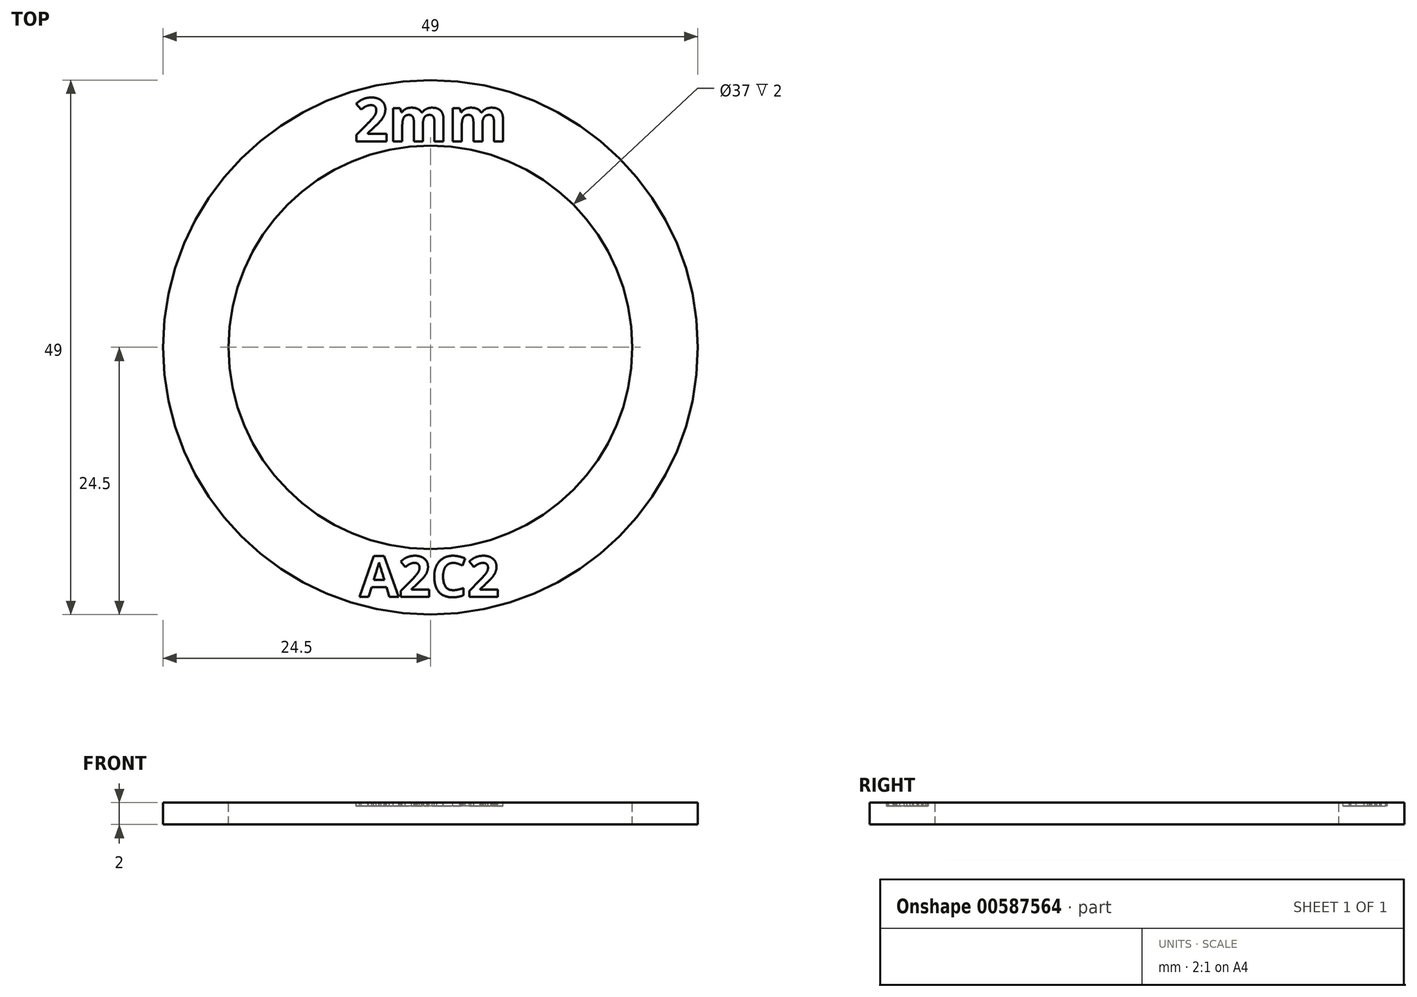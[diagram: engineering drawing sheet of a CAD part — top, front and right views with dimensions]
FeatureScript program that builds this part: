
annotation { "Feature Type Name" : "Feature", "Feature Type Description" : "" }
export const myFeature = defineFeature(function(context is Context, id is Id, definition is map)
    precondition{}
    {
        {
            var Q0;
            Q0=qCreatedBy(makeId("Top.planeOp"),FACE);
            var sketch = newSketch(context, id + "F0", { "sketchPlane" : qUnion([Q0])});
            skCircle(sketch, "E0", {"center": v(0, 0) * mm, "radius": 24.5 * mm});
            skCircle(sketch, "E1", {"center": v(0, 0) * mm, "radius": 18.5 * mm});
            skText(sketch, "E2", { "text": "A2C2", "fontName": "OpenSans-Bold.ttf"});
            skText(sketch, "E3", { "text": "2mm", "fontName": "OpenSans-Bold.ttf"});
            const initialGuessF0  = {"E2": [-0.0065, -0.02287, 1, 0, 0.00374], "E3": [-0.00701, 0.01888, 1, 0, 0.004]};
            skSetInitialGuess(sketch, initialGuessF0);
            skSolve(sketch);
        }
        {
            var Q0;
            Q0 = qSketchRegion(id + "F0", true);
            var Q1;
            Q1=makeQuery(id+"F0.imprint","IMPRINT",FACE,{"disambiguationData":[TD([[makeQuery(id+"F0.imprint","IMPRINT",EDGE,{"derivedFrom":sQuery(id+"F0.wireOp",EDGE,"E2.sketch_text.stroke-0")}),-1.0]])]});
            var Q2;
            Q2=makeQuery(id+"F0.imprint","IMPRINT",FACE,{"disambiguationData":[TD([[makeQuery(id+"F0.imprint","IMPRINT",EDGE,{"derivedFrom":sQuery(id+"F0.wireOp",EDGE,"E2.sketch_text.stroke-8")}),1.0]])]});
            var Q3;
            Q3=makeQuery(id+"F0.imprint","IMPRINT",FACE,{"disambiguationData":[TD([[makeQuery(id+"F0.imprint","IMPRINT",EDGE,{"derivedFrom":sQuery(id+"F0.wireOp",EDGE,"E2.sketch_text.stroke-12")}),-1.0]])]});
            var Q4;
            Q4=makeQuery(id+"F0.imprint","IMPRINT",FACE,{"disambiguationData":[TD([[makeQuery(id+"F0.imprint","IMPRINT",EDGE,{"derivedFrom":sQuery(id+"F0.wireOp",EDGE,"E2.sketch_text.stroke-36")}),-1.0]])]});
            var Q5;
            Q5=makeQuery(id+"F0.imprint","IMPRINT",FACE,{"disambiguationData":[TD([[makeQuery(id+"F0.imprint","IMPRINT",EDGE,{"derivedFrom":sQuery(id+"F0.wireOp",EDGE,"E2.sketch_text.stroke-51")}),-1.0]])]});
            var Q6;
            Q6=makeQuery(id+"F0.imprint","IMPRINT",FACE,{"disambiguationData":[TD([[makeQuery(id+"F0.imprint","IMPRINT",EDGE,{"derivedFrom":sQuery(id+"F0.wireOp",EDGE,"E3.sketch_text.stroke-0")}),-1.0]])]});
            var Q7;
            Q7=makeQuery(id+"F0.imprint","IMPRINT",FACE,{"disambiguationData":[TD([[makeQuery(id+"F0.imprint","IMPRINT",EDGE,{"derivedFrom":sQuery(id+"F0.wireOp",EDGE,"E3.sketch_text.stroke-24")}),-1.0]])]});
            var Q8;
            Q8=makeQuery(id+"F0.imprint","IMPRINT",FACE,{"disambiguationData":[TD([[makeQuery(id+"F0.imprint","IMPRINT",EDGE,{"derivedFrom":sQuery(id+"F0.wireOp",EDGE,"E3.sketch_text.stroke-52")}),-1.0]])]});
            extrude(context, id + "F1", {"entities" : qUnion([Q0, Q1, Q2, Q3, Q4, Q5, Q6, Q7, Q8]), "oppositeDirection" : true, "depth" : 2 * mm, "offsetDistance" : 25 * mm});
        }
        {
            var Q0;
            Q0=makeQuery(id+"F0.imprint","IMPRINT",FACE,{"disambiguationData":[TD([[makeQuery(id+"F0.imprint","IMPRINT",EDGE,{"derivedFrom":sQuery(id+"F0.wireOp",EDGE,"E2.sketch_text.stroke-12")}),-1.0]])]});
            var Q1;
            Q1=makeQuery(id+"F0.imprint","IMPRINT",FACE,{"disambiguationData":[TD([[makeQuery(id+"F0.imprint","IMPRINT",EDGE,{"derivedFrom":sQuery(id+"F0.wireOp",EDGE,"E2.sketch_text.stroke-0")}),-1.0]])]});
            var Q2;
            Q2=makeQuery(id+"F0.imprint","IMPRINT",FACE,{"disambiguationData":[TD([[makeQuery(id+"F0.imprint","IMPRINT",EDGE,{"derivedFrom":sQuery(id+"F0.wireOp",EDGE,"E2.sketch_text.stroke-36")}),-1.0]])]});
            var Q3;
            Q3=makeQuery(id+"F0.imprint","IMPRINT",FACE,{"disambiguationData":[TD([[makeQuery(id+"F0.imprint","IMPRINT",EDGE,{"derivedFrom":sQuery(id+"F0.wireOp",EDGE,"E2.sketch_text.stroke-51")}),-1.0]])]});
            var Q4;
            Q4=makeQuery(id+"F0.imprint","IMPRINT",FACE,{"disambiguationData":[TD([[makeQuery(id+"F0.imprint","IMPRINT",EDGE,{"derivedFrom":sQuery(id+"F0.wireOp",EDGE,"E3.sketch_text.stroke-0")}),-1.0]])]});
            var Q5;
            Q5=makeQuery(id+"F0.imprint","IMPRINT",FACE,{"disambiguationData":[TD([[makeQuery(id+"F0.imprint","IMPRINT",EDGE,{"derivedFrom":sQuery(id+"F0.wireOp",EDGE,"E3.sketch_text.stroke-24")}),-1.0]])]});
            var Q6;
            Q6=makeQuery(id+"F0.imprint","IMPRINT",FACE,{"disambiguationData":[TD([[makeQuery(id+"F0.imprint","IMPRINT",EDGE,{"derivedFrom":sQuery(id+"F0.wireOp",EDGE,"E3.sketch_text.stroke-52")}),-1.0]])]});
            extrude(context, id + "F2", {"entities" : qUnion([Q0, Q1, Q2, Q3, Q4, Q5, Q6]), "operationType" : NewBodyOperationType.REMOVE, "oppositeDirection" : true, "depth" : 0.3 * mm, "offsetDistance" : 25 * mm});
        }
    });
